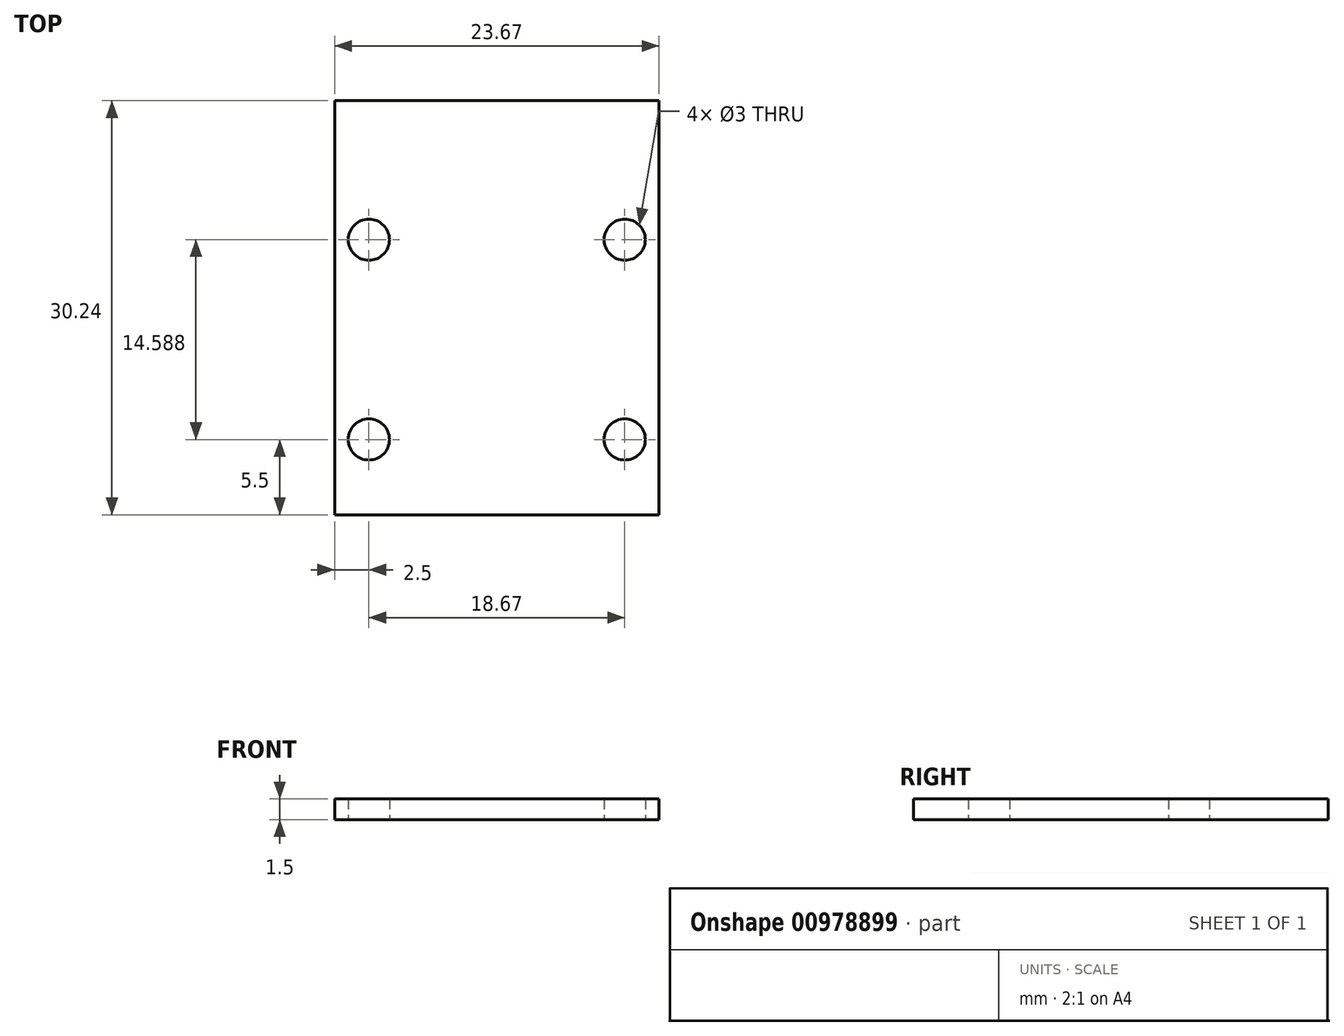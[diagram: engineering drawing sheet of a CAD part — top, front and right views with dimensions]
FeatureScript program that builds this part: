
annotation { "Feature Type Name" : "Feature", "Feature Type Description" : "" }
export const myFeature = defineFeature(function(context is Context, id is Id, definition is map)
    precondition{}
    {
        {
            var Q0;
            Q0=qCreatedBy(makeId("Top.planeOp"),FACE);
            var sketch = newSketch(context, id + "F0", { "sketchPlane" : qUnion([Q0])});
            skLineSegment(sketch, "E0.bottom", {"start": v(-23.67, 39.6) * mm, "end": v(0, 39.6) * mm});
            skLineSegment(sketch, "E0.top", {"start": v(-23.67, 9.36) * mm, "end": v(0, 9.36) * mm});
            skLineSegment(sketch, "E0.left", {"start": v(-23.67, 39.6) * mm, "end": v(-23.67, 9.36) * mm});
            skLineSegment(sketch, "E0.right", {"start": v(0, 39.6) * mm, "end": v(0, 9.36) * mm});
            skCircle(sketch, "E1", {"center": v(-21.17, 29.45) * mm, "radius": 1.5 * mm});
            skCircle(sketch, "E2", {"center": v(-2.5, 29.45) * mm, "radius": 1.5 * mm});
            skLineSegment(sketch, "E3", {"start": v(-23.67, 9.36) * mm, "end": v(-23.67, 13.36) * mm});
            skLineSegment(sketch, "E4", {"start": v(-23.67, 13.36) * mm, "end": v(-23.67, 14.86) * mm});
            skCircle(sketch, "E5", {"center": v(-21.17, 14.86) * mm, "radius": 1.5 * mm});
            skCircle(sketch, "E6", {"center": v(-2.5, 14.86) * mm, "radius": 1.5 * mm});
            skSolve(sketch);
        }
        {
            var Q0;
            Q0 = qSketchRegion(id + "F0", true);
            var Q1;
            Q1=makeQuery(id+"F0.imprint","IMPRINT",FACE,{"disambiguationData":[TD([[makeQuery(id+"F0.imprint","IMPRINT",EDGE,{"derivedFrom":sQuery(id+"F0.wireOp",EDGE,"E0.bottom")}),-1.0]])]});
            extrude(context, id + "F1", {"entities" : qUnion([Q0, Q1]), "depth" : 1.5 * mm, "offsetDistance" : 25 * mm});
        }
    });
